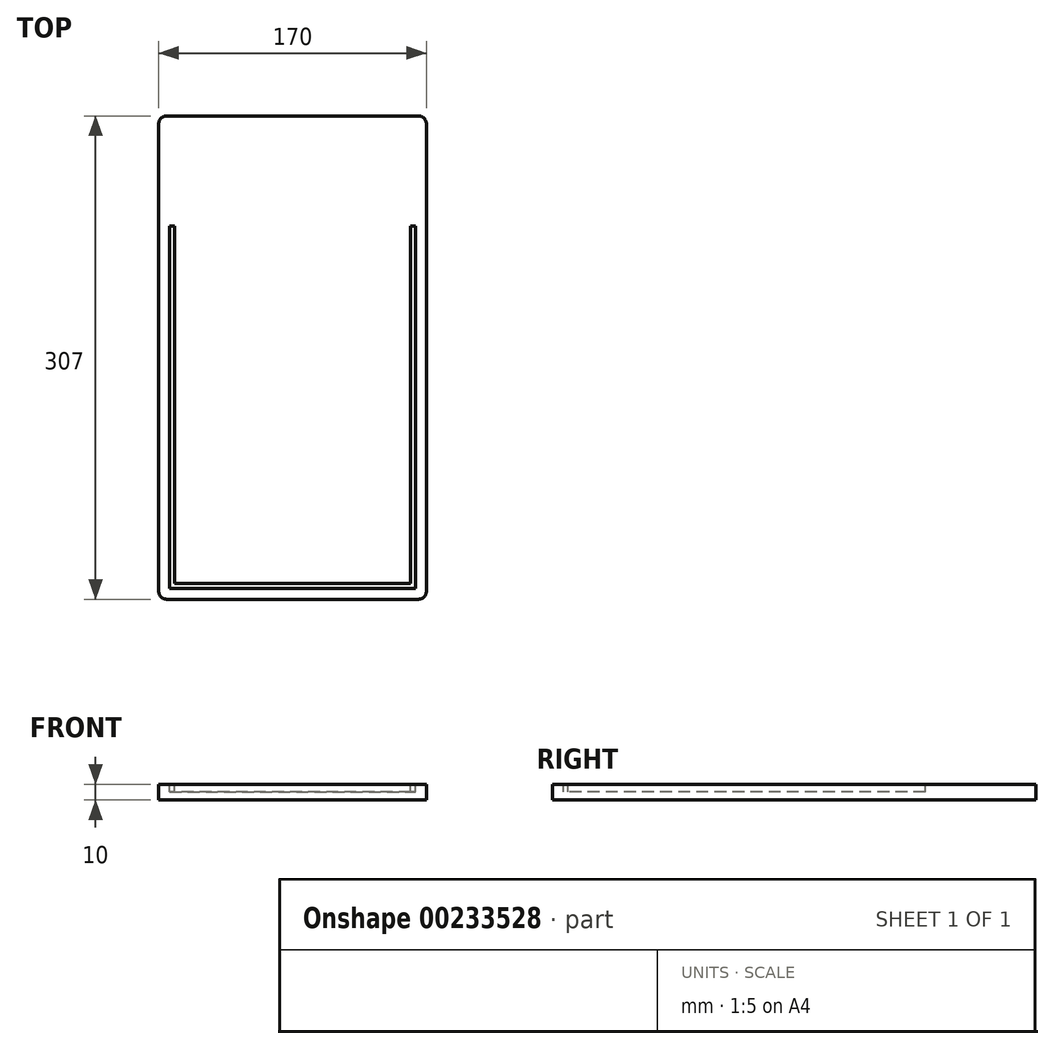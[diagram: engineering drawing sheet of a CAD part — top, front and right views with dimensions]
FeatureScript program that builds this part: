
annotation { "Feature Type Name" : "Feature", "Feature Type Description" : "" }
export const myFeature = defineFeature(function(context is Context, id is Id, definition is map)
    precondition{}
    {
        {
            var Q0;
            Q0=qCreatedBy(makeId("Top.planeOp"),FACE);
            var sketch = newSketch(context, id + "F0", { "sketchPlane" : qUnion([Q0])});
            skLineSegment(sketch, "E0.bottom", {"start": v(80, 153.5) * mm, "end": v(-80, 153.5) * mm});
            skLineSegment(sketch, "E0.top", {"start": v(80, -153.5) * mm, "end": v(-80, -153.5) * mm});
            skLineSegment(sketch, "E0.left", {"start": v(85, 148.5) * mm, "end": v(85, -148.5) * mm});
            skLineSegment(sketch, "E0.right", {"start": v(-85, 148.5) * mm, "end": v(-85, -148.5) * mm});
            skPoint(sketch, "E0.middle", {"position": v(0, 0) * mm});
            skPoint(sketch, "E1.visualSharp", {"position": v(-85, 153.5) * mm});
            skArc(sketch, "E1.filletArc", {"start": v(-80, 153.5) * mm, "mid": v(-83.54, 152.04) * mm, "end": v(-85, 148.5) * mm});
            skPoint(sketch, "E2.visualSharp", {"position": v(85, 153.5) * mm});
            skArc(sketch, "E2.filletArc", {"start": v(85, 148.5) * mm, "mid": v(83.54, 152.04) * mm, "end": v(80, 153.5) * mm});
            skPoint(sketch, "E3.visualSharp", {"position": v(-85, -153.5) * mm});
            skArc(sketch, "E3.filletArc", {"start": v(-85, -148.5) * mm, "mid": v(-83.54, -152.04) * mm, "end": v(-80, -153.5) * mm});
            skPoint(sketch, "E4.visualSharp", {"position": v(85, -153.5) * mm});
            skArc(sketch, "E4.filletArc", {"start": v(80, -153.5) * mm, "mid": v(83.54, -152.04) * mm, "end": v(85, -148.5) * mm});
            skLineSegment(sketch, "E5", {"start": v(-78, 83.5) * mm, "end": v(-78, -146.5) * mm});
            skLineSegment(sketch, "E6", {"start": v(-78, -146.5) * mm, "end": v(78, -146.5) * mm});
            skLineSegment(sketch, "E7", {"start": v(78, -146.5) * mm, "end": v(78, 83.5) * mm});
            skLineSegment(sketch, "E8", {"start": v(78, 83.5) * mm, "end": v(75, 83.5) * mm});
            skLineSegment(sketch, "E9", {"start": v(75, 83.5) * mm, "end": v(75, -143.5) * mm});
            skLineSegment(sketch, "E10", {"start": v(75, -143.5) * mm, "end": v(-75, -143.5) * mm});
            skLineSegment(sketch, "E11", {"start": v(-75, -143.5) * mm, "end": v(-75, 83.5) * mm});
            skLineSegment(sketch, "E12", {"start": v(-75, 83.5) * mm, "end": v(-78, 83.5) * mm});
            skLineSegment(sketch, "E13", {"start": v(0, 75.67) * mm, "end": v(0, -79.3) * mm, "construction": true});
            skLineSegment(sketch, "E14", {"start": v(-75, -143.5) * mm, "end": v(-75, -146.5) * mm, "construction": true});
            skSolve(sketch);
        }
        {
            var Q0;
            Q0=makeQuery(id+"F0.imprint","IMPRINT",FACE,{"disambiguationData":[TD([[makeQuery(id+"F0.imprint","IMPRINT",EDGE,{"derivedFrom":sQuery(id+"F0.wireOp",EDGE,"E0.bottom")}),1.0]])]});
            var Q1;
            Q1=makeQuery(id+"F0.imprint","IMPRINT",FACE,{"disambiguationData":[TD([[makeQuery(id+"F0.imprint","IMPRINT",EDGE,{"derivedFrom":sQuery(id+"F0.wireOp",EDGE,"E5")}),1.0]])]});
            extrude(context, id + "F1", {"entities" : qUnion([Q0, Q1]), "oppositeDirection" : true, "depth" : 10 * mm});
        }
        {
            var Q0;
            Q0=makeQuery(id+"F0.imprint","IMPRINT",FACE,{"disambiguationData":[TD([[makeQuery(id+"F0.imprint","IMPRINT",EDGE,{"derivedFrom":sQuery(id+"F0.wireOp",EDGE,"E5")}),1.0]])]});
            extrude(context, id + "F2", {"entities" : qUnion([Q0]), "operationType" : NewBodyOperationType.REMOVE, "oppositeDirection" : true, "depth" : 5 * mm});
        }
    });
